# Revit family: Кран для слива и наполнения котла 2512 11
name_source: partatom
category: Rohrzubehör
revit_build: Autodesk Revit 2018 (Build: 20190510_1515(x64)
units: mm (PartAtom-declared; Revit-internal decimal feet)

## family parameters
Arbeitsebenenbasiert = Nein
Beim Laden mit Abzugskörper schneiden = Nein
Bemaßung runder Anschluss = Durchmesser verwenden
Gemeinsam genutzt = Nein
Immer vertikal = Ja
OmniClass-Nummer = 23.65.55.14
OmniClass-Titel = Valves for Liquid Services
Teiletyp = Normal

## types (1)
- Кран для слива и наполнения котла 2512 11
    D02 = 9.3 mm  [stored 0.0305118 ft]
    D03 = 11.7 mm  [stored 0.0383858 ft]
    D04 = 11.1 mm  [stored 0.0364173 ft]
    D05 = 13.4 mm  [stored 0.0439633 ft]
    D06 = 12.1 mm
    D07 = 14.5 mm  [stored 0.0475722 ft]
    D08 = 7 mm  [stored 0.0229659 ft]
    G02 = 13.2 mm  [stored 0.0433071 ft]
    H00 = 17 mm
    Hersteller = Herz-Armaturen GmbH
    L00 = 44 mm  [stored 0.144357 ft]
    L01 = 19.5 mm  [stored 0.0639764 ft]
    L02 = 13 mm
    L03 = 8.5 mm  [stored 0.0278871 ft]
    L04 = 9.5 mm  [stored 0.031168 ft]
    L05 = 6.5 mm
    L06 = 19 mm  [stored 0.062336 ft]
    L07 = 4 mm  [stored 0.0131234 ft]
    L08 = 8 mm  [stored 0.0262467 ft]
    L09 = 13.5 mm  [stored 0.0442913 ft]
    L10 = 14 mm  [stored 0.0459318 ft]
    R01 = 7 mm  [stored 0.0229659 ft]
    R99 = 2 mm  [stored 0.00656168 ft]
    S01 = 51 mm  [stored 0.167323 ft]
    S02 = 24.5 mm
    S03 = 16 mm  [stored 0.0524934 ft]
    S04 = 45 mm  [stored 0.147638 ft]
    SCRNCODE = 05;08;01
    SCRNSEQ = ARM;ARM_TYP="ABSV";1
    SCTWCODE = 01;10;01
    SCTWSEQ = ENT;AO;1
    URL = www.herz-armaturen.ru
    Корпус = штампованная латунь, CW617N
    Макс. рабочая температура = 110 °C
    Макс. рабочее давление = 1000000.0 Pa
    Мин. рабочая температура = -30 °C
    Область применения = Краны используются для слива и наполнения котла в инженерных системах зданий: в системах отопления или холодоснабжения. Ароматические хлорированные углеводороды, такие как природный газ или продукты нефтепереработки, разрушают уплотнения из EPDM.
    Среда = Качество теплоносителя в соответствии с ÖNORM H5195 и/или предписаниями VDI-Standard 2035. Разрешается использование смеси этилен или пропиленгликоля в соотношении 25-50% с водой.
    Уплотнения = Шар: PTFE, шпиндель: PTFE
    Шар = штампованная латунь, CW617N, хромированный, полнопроходной шар
    Шпиндель = Латунь CW614N

note: [stored X ft] marks values corroborated as IEEE doubles in the binary element streams (Revit-internal decimal feet)
